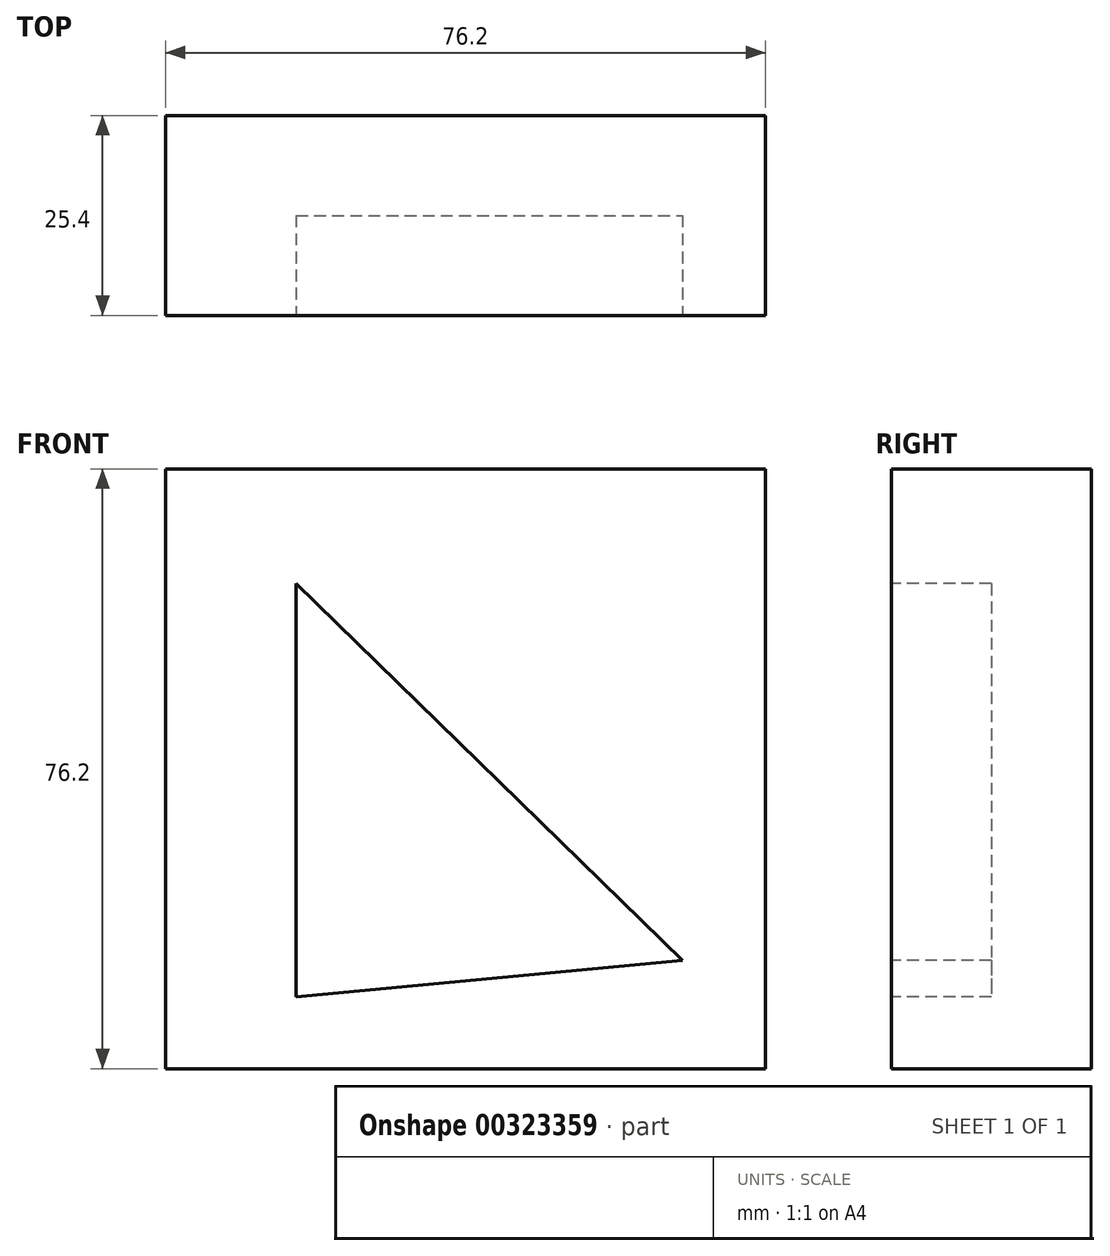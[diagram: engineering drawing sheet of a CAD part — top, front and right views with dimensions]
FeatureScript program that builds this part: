
annotation { "Feature Type Name" : "Feature", "Feature Type Description" : "" }
export const myFeature = defineFeature(function(context is Context, id is Id, definition is map)
    precondition{}
    {
        {
            var Q0;
            Q0=qCreatedBy(makeId("Front.planeOp"),FACE);
            var sketch = newSketch(context, id + "F0", { "sketchPlane" : qUnion([Q0])});
            skLineSegment(sketch, "E0", {"start": v(0, 0) * mm, "end": v(0, 76.2) * mm});
            skLineSegment(sketch, "E1", {"start": v(0, 76.2) * mm, "end": v(76.2, 76.2) * mm});
            skLineSegment(sketch, "E2", {"start": v(76.2, 76.2) * mm, "end": v(76.2, 0) * mm});
            skLineSegment(sketch, "E3", {"start": v(76.2, 0) * mm, "end": v(0, 0) * mm});
            skSolve(sketch);
        }
        {
            var Q0;
            Q0 = qSketchRegion(id + "F0", true);
            extrude(context, id + "F1", {"entities" : qUnion([Q0]), "depth" : 25.4 * mm});
        }
        {
            var Q0;
            Q0=makeQuery(id+"F1.opExtrude","CAP_FACE",FACE,{"disambiguationData":[OSD([sQuery(id+"F0.wireOp",EDGE,"E0"),sQuery(id+"F0.wireOp",EDGE,"E1"),sQuery(id+"F0.wireOp",EDGE,"E2"),sQuery(id+"F0.wireOp",EDGE,"E3")])],"isStart":false});
            var sketch = newSketch(context, id + "F2", { "sketchPlane" : qUnion([Q0])});
            skLineSegment(sketch, "E4", {"start": v(16.57, 61.62) * mm, "end": v(16.57, 9.1) * mm});
            skLineSegment(sketch, "E5", {"start": v(16.57, 61.62) * mm, "end": v(65.66, 13.74) * mm});
            skLineSegment(sketch, "E6", {"start": v(65.66, 13.74) * mm, "end": v(16.57, 9.1) * mm});
            skSolve(sketch);
        }
        {
            var Q0;
            Q0=makeQuery(id+"F2.imprint","IMPRINT",FACE,{"disambiguationData":[TD([[makeQuery(id+"F2.imprint","IMPRINT",EDGE,{"derivedFrom":sQuery(id+"F2.wireOp",EDGE,"E4")}),1.0]])]});
            extrude(context, id + "F3", {"entities" : qUnion([Q0]), "operationType" : NewBodyOperationType.REMOVE, "oppositeDirection" : true, "depth" : 12.7 * mm});
        }
    });
